# Revit family: Lighting_Device-Daylight_Harvesting-Hubbell_Wiring-DH
name_source: partatom
category: Lighting Devices
revit_build: Autodesk Revit 2015 (Build: 20140606_1530(x64)
units: mm (PartAtom-declared; Revit-internal decimal feet)

## types (4) — shared parameters
Apparent Load = 0 VA
Certifications = cULus listed to UL 773A
Connector Description 1 = Power Supply
Connector Description 2 = Controls
Default Elevation = 48 "
Load Classification = Other
Manufacturer = Hubbell Wiring Device-Kellems
Number of Poles = 1
Operating Temperature = -13°F to +140°F (-11°C – 60°C)
Power Factor = 1
Product Documentation Link = http://ecatalog.hubbell-wiring.com
Product Material = Plastic - Hubbell - White
Product Page URL = http://www.hubbell-wiring.com
Product data url = https://bimobject.com
Sensor Type = Blue-enhanced photo diode
URL = http://www.hubbell-wiring.com
Voltage = 120 V

## per-type parameters (varying)
| type | Daylight Harvesting | Description | Lens Filter | Model |
| DHIP | DHIP : Indoor Photocell Sensor | Skylight Photocell Sensor Min. = 2 fc. / Factory Set Max. = 1000 fc. | Glass - Hubbell - Dome Opaque | DHSP |
| DHOP | DHOP : Outdoor Photocell Sensor | Outdoor Photocell Sensor Min. = 0 fc. / Factory Set Max. = 250 fc. | Glass - Hubbell - Dome Opaque | DHOP |
| DHAP | DHAP : Atrium Photocell Sensor | Atrium Photocell Sensor Min. = 2 fc. / Factory Set Max. = 1000 fc. | Glass - Hubbell - Dome Opaque | DHAP |
| DHSP | DHSP : Skylight Photocell Sensor | Skylight Photocell Sensor Min. = 2 fc. / Factory Set Max. = 1000 fc. | Glass - Hubbell - Fresnel Clear | DHSP |

## geometry (parser evidence)
native form markers: Blend x2, Sweep x12
no freeform markers — native parametric forms only
